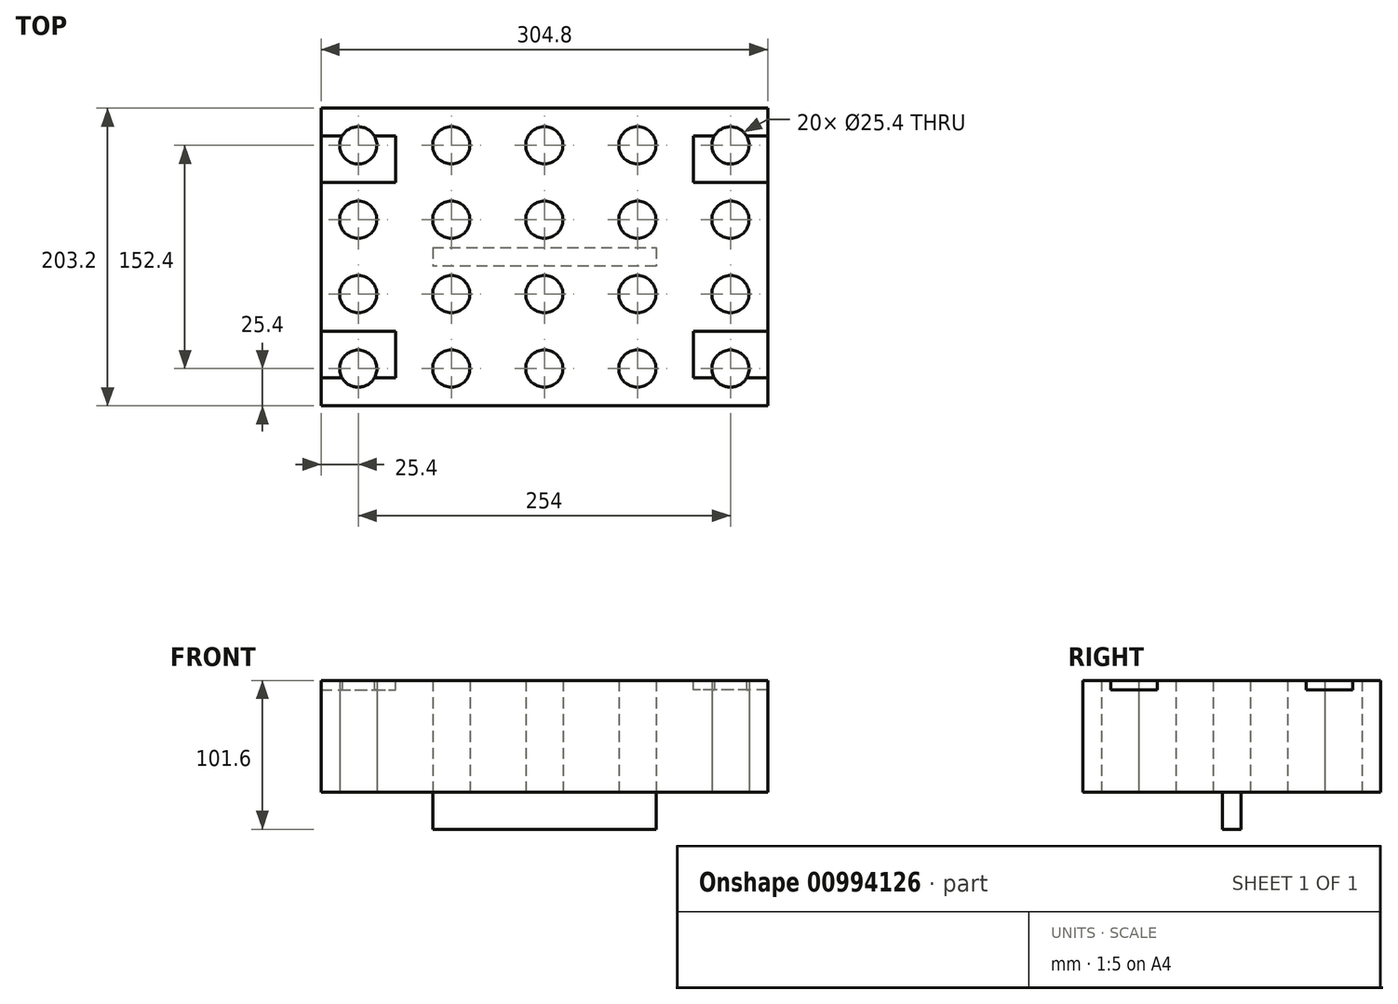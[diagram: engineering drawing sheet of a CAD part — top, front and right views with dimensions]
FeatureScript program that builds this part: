
annotation { "Feature Type Name" : "Feature", "Feature Type Description" : "" }
export const myFeature = defineFeature(function(context is Context, id is Id, definition is map)
    precondition{}
    {
        {
            var Q0;
            Q0=qCreatedBy(makeId("Top.planeOp"),FACE);
            var sketch = newSketch(context, id + "F0", { "sketchPlane" : qUnion([Q0])});
            skLineSegment(sketch, "E0.bottom", {"start": v(-152.4, 101.6) * mm, "end": v(152.4, 101.6) * mm});
            skLineSegment(sketch, "E0.top", {"start": v(-152.4, -101.6) * mm, "end": v(152.4, -101.6) * mm});
            skLineSegment(sketch, "E0.left", {"start": v(-152.4, 101.6) * mm, "end": v(-152.4, -101.6) * mm});
            skLineSegment(sketch, "E0.right", {"start": v(152.4, 101.6) * mm, "end": v(152.4, -101.6) * mm});
            skPoint(sketch, "E0.middle", {"position": v(0, 0) * mm});
            skCircle(sketch, "E1", {"center": v(-127, -76.2) * mm, "radius": 12.7 * mm});
            skCircle(sketch, "E2", {"center": v(-127, -25.4) * mm, "radius": 12.7 * mm});
            skCircle(sketch, "E3", {"center": v(-127, 76.2) * mm, "radius": 12.7 * mm});
            skCircle(sketch, "E4", {"center": v(-127, 25.4) * mm, "radius": 12.7 * mm});
            skLineSegment(sketch, "E5", {"start": v(0, -101.6) * mm, "end": v(0, 101.6) * mm, "construction": true});
            skLineSegment(sketch, "E6", {"start": v(-127, -25.4) * mm, "end": v(-127, 25.4) * mm});
            skLineSegment(sketch, "E7", {"start": v(-127, 0) * mm, "end": v(0, 0) * mm, "construction": true});
            skLineSegment(sketch, "E8", {"start": v(-63.5, 0) * mm, "end": v(-63.5, -101.6) * mm, "construction": true});
            skLineSegment(sketch, "E9", {"start": v(-127, -76.2) * mm, "end": v(-63.5, -76.2) * mm, "construction": true});
            skLineSegment(sketch, "E10", {"start": v(-95.25, -76.2) * mm, "end": v(-95.25, 0) * mm, "construction": true});
            skPoint(sketch, "E10.endSnap0", {"position": v(-95.25, -76.2) * mm});
            skCircle(sketch, "E11.MirrorC", {"center": v(-63.5, -76.2) * mm, "radius": 12.7 * mm});
            skCircle(sketch, "E12.MirrorC", {"center": v(-63.5, -25.4) * mm, "radius": 12.7 * mm});
            skCircle(sketch, "E13.MirrorC", {"center": v(-63.5, 25.4) * mm, "radius": 12.7 * mm});
            skCircle(sketch, "E14.MirrorC", {"center": v(-63.5, 76.2) * mm, "radius": 12.7 * mm});
            skCircle(sketch, "E15.MirrorC", {"center": v(0, -76.2) * mm, "radius": 12.7 * mm});
            skCircle(sketch, "E16.MirrorC", {"center": v(0, -25.4) * mm, "radius": 12.7 * mm});
            skCircle(sketch, "E17.MirrorC", {"center": v(0, 25.4) * mm, "radius": 12.7 * mm});
            skCircle(sketch, "E18.MirrorC", {"center": v(0, 76.2) * mm, "radius": 12.7 * mm});
            skCircle(sketch, "E19.MirrorC", {"center": v(63.5, -76.2) * mm, "radius": 12.7 * mm});
            skCircle(sketch, "E20.MirrorC", {"center": v(127, -76.2) * mm, "radius": 12.7 * mm});
            skCircle(sketch, "E21.MirrorC", {"center": v(127, -25.4) * mm, "radius": 12.7 * mm});
            skCircle(sketch, "E22.MirrorC", {"center": v(63.5, 25.4) * mm, "radius": 12.7 * mm});
            skCircle(sketch, "E23.MirrorC", {"center": v(127, 25.4) * mm, "radius": 12.7 * mm});
            skCircle(sketch, "E24.MirrorC", {"center": v(127, 76.2) * mm, "radius": 12.7 * mm});
            skCircle(sketch, "E25.MirrorC", {"center": v(63.5, 76.2) * mm, "radius": 12.7 * mm});
            skCircle(sketch, "E26.MirrorC", {"center": v(63.5, -25.4) * mm, "radius": 12.7 * mm});
            skSolve(sketch);
        }
        {
            var Q0;
            Q0 = qSketchRegion(id + "F0", true);
            extrude(context, id + "F1", {"entities" : qUnion([Q0]), "depth" : 76.2 * mm, "offsetDistance" : 25.4 * mm});
        }
        {
            var Q0;
            Q0=makeQuery(id+"F1.opExtrude","CAP_FACE",FACE,{"disambiguationData":[OSD([sQuery(id+"F0.wireOp",EDGE,"E0.bottom"),sQuery(id+"F0.wireOp",EDGE,"E0.top"),sQuery(id+"F0.wireOp",EDGE,"E0.left"),sQuery(id+"F0.wireOp",EDGE,"E0.right")])],"isStart":true});
            var sketch = newSketch(context, id + "F2", { "sketchPlane" : qUnion([Q0])});
            skLineSegment(sketch, "E27", {"start": v(-76.2, -6.35) * mm, "end": v(76.2, -6.35) * mm});
            skLineSegment(sketch, "E28", {"start": v(76.2, -6.35) * mm, "end": v(76.2, 6.35) * mm});
            skLineSegment(sketch, "E29", {"start": v(76.2, 6.35) * mm, "end": v(-76.2, 6.35) * mm});
            skLineSegment(sketch, "E30", {"start": v(-76.2, -6.35) * mm, "end": v(-76.2, 6.35) * mm});
            skSolve(sketch);
        }
        {
            var Q0;
            Q0 = qSketchRegion(id + "F2", true);
            extrude(context, id + "F3", {"entities" : qUnion([Q0]), "operationType" : NewBodyOperationType.ADD, "depth" : 25.4 * mm, "offsetDistance" : 25.4 * mm});
        }
        {
            var Q0;
            Q0=makeQuery(id+"F1.opExtrude","CAP_FACE",FACE,{"disambiguationData":[OSD([sQuery(id+"F0.wireOp",EDGE,"E0.bottom"),sQuery(id+"F0.wireOp",EDGE,"E0.top"),sQuery(id+"F0.wireOp",EDGE,"E0.left"),sQuery(id+"F0.wireOp",EDGE,"E0.right"),sQuery(id+"F0.wireOp",EDGE,"E1"),sQuery(id+"F0.wireOp",EDGE,"E2"),sQuery(id+"F0.wireOp",EDGE,"E3"),sQuery(id+"F0.wireOp",EDGE,"E4"),sQuery(id+"F0.wireOp",EDGE,"E11.MirrorC"),sQuery(id+"F0.wireOp",EDGE,"E12.MirrorC"),sQuery(id+"F0.wireOp",EDGE,"E13.MirrorC"),sQuery(id+"F0.wireOp",EDGE,"E14.MirrorC"),sQuery(id+"F0.wireOp",EDGE,"E15.MirrorC"),sQuery(id+"F0.wireOp",EDGE,"E16.MirrorC"),sQuery(id+"F0.wireOp",EDGE,"E17.MirrorC"),sQuery(id+"F0.wireOp",EDGE,"E18.MirrorC"),sQuery(id+"F0.wireOp",EDGE,"E19.MirrorC"),sQuery(id+"F0.wireOp",EDGE,"E20.MirrorC"),sQuery(id+"F0.wireOp",EDGE,"E21.MirrorC"),sQuery(id+"F0.wireOp",EDGE,"E22.MirrorC"),sQuery(id+"F0.wireOp",EDGE,"E23.MirrorC"),sQuery(id+"F0.wireOp",EDGE,"E24.MirrorC"),sQuery(id+"F0.wireOp",EDGE,"E25.MirrorC"),sQuery(id+"F0.wireOp",EDGE,"E26.MirrorC")])],"isStart":false});
            var sketch = newSketch(context, id + "F4", { "sketchPlane" : qUnion([Q0])});
            skLineSegment(sketch, "E31.bottom", {"start": v(-152.4, 82.55) * mm, "end": v(-101.6, 82.55) * mm});
            skLineSegment(sketch, "E31.top", {"start": v(-152.4, 50.8) * mm, "end": v(-101.6, 50.8) * mm});
            skLineSegment(sketch, "E31.left", {"start": v(-152.4, 82.55) * mm, "end": v(-152.4, 50.8) * mm});
            skLineSegment(sketch, "E31.right", {"start": v(-101.6, 82.55) * mm, "end": v(-101.6, 50.8) * mm});
            skLineSegment(sketch, "E32.bottom", {"start": v(-152.4, -50.8) * mm, "end": v(-101.6, -50.8) * mm});
            skLineSegment(sketch, "E32.top", {"start": v(-152.4, -82.55) * mm, "end": v(-101.6, -82.55) * mm});
            skLineSegment(sketch, "E32.left", {"start": v(-152.4, -50.8) * mm, "end": v(-152.4, -82.55) * mm});
            skLineSegment(sketch, "E32.right", {"start": v(-101.6, -50.8) * mm, "end": v(-101.6, -82.55) * mm});
            skLineSegment(sketch, "E33", {"start": v(0, 101.6) * mm, "end": v(0, -101.6) * mm, "construction": true});
            skLineSegment(sketch, "E34.MirrorCS", {"start": v(152.4, 50.8) * mm, "end": v(101.6, 50.8) * mm});
            skLineSegment(sketch, "E35.MirrorCS", {"start": v(152.4, 82.55) * mm, "end": v(152.4, 50.8) * mm});
            skLineSegment(sketch, "E36.MirrorCS", {"start": v(152.4, 82.55) * mm, "end": v(101.6, 82.55) * mm});
            skLineSegment(sketch, "E37.MirrorCS", {"start": v(101.6, 82.55) * mm, "end": v(101.6, 50.8) * mm});
            skLineSegment(sketch, "E38.MirrorCS", {"start": v(101.6, -50.8) * mm, "end": v(101.6, -82.55) * mm});
            skLineSegment(sketch, "E39.MirrorCS", {"start": v(152.4, -50.8) * mm, "end": v(101.6, -50.8) * mm});
            skLineSegment(sketch, "E40.MirrorCS", {"start": v(152.4, -50.8) * mm, "end": v(152.4, -82.55) * mm});
            skLineSegment(sketch, "E41.MirrorCS", {"start": v(152.4, -82.55) * mm, "end": v(101.6, -82.55) * mm});
            skSolve(sketch);
        }
        {
            var Q0;
            Q0 = qSketchRegion(id + "F4", true);
            extrude(context, id + "F5", {"entities" : qUnion([Q0]), "operationType" : NewBodyOperationType.REMOVE, "oppositeDirection" : true, "depth" : 6.35 * mm, "offsetDistance" : 25.4 * mm});
        }
    });
